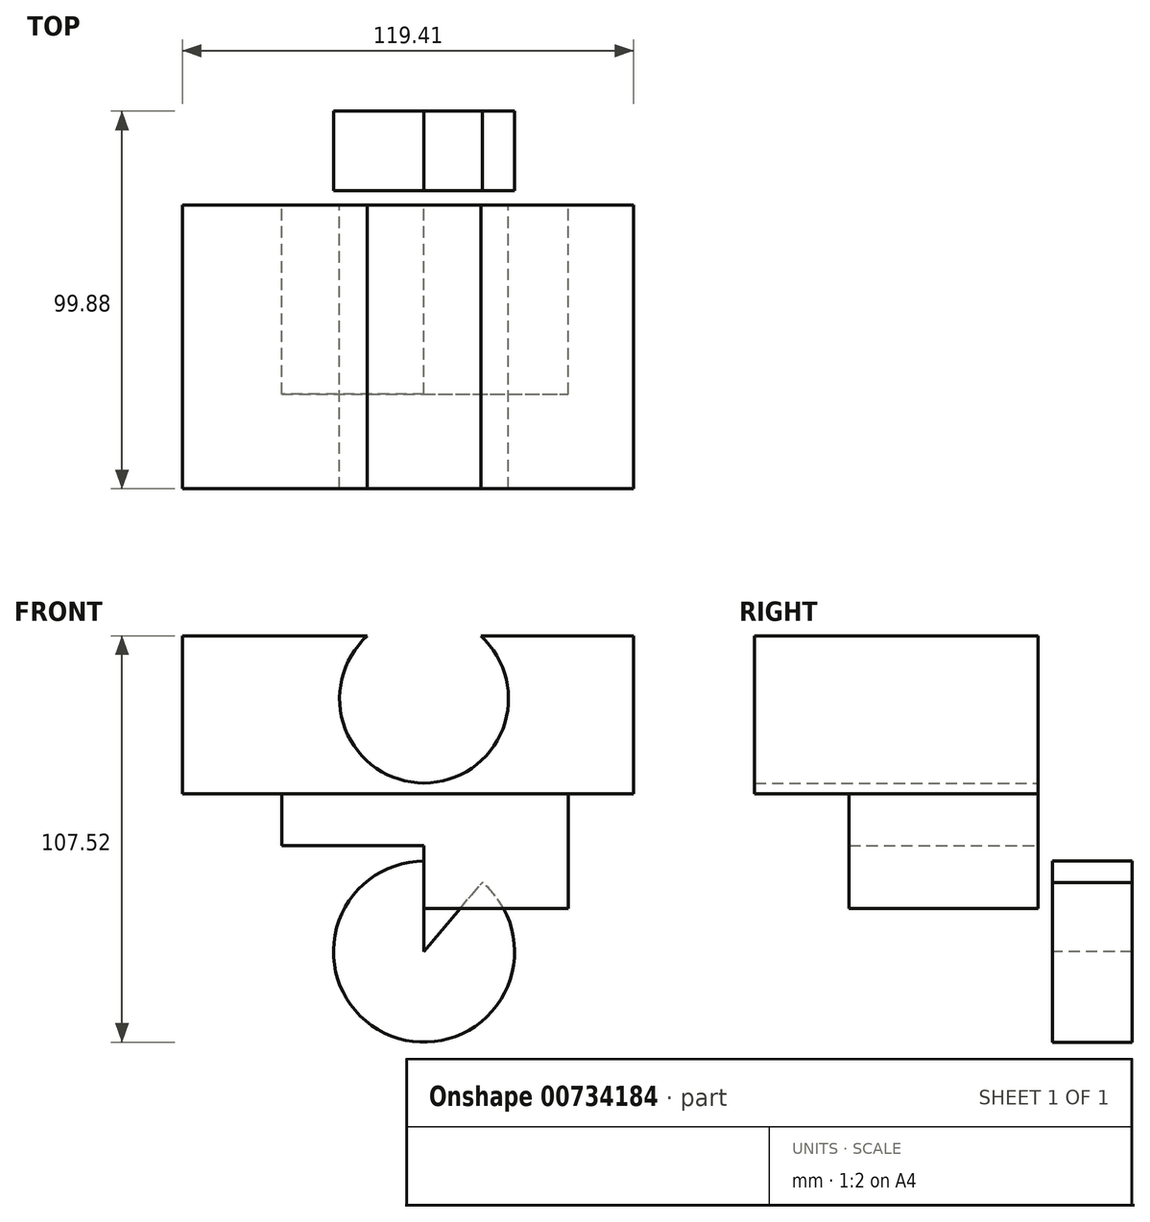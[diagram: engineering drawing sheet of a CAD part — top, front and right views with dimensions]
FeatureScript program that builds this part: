
annotation { "Feature Type Name" : "Feature", "Feature Type Description" : "" }
export const myFeature = defineFeature(function(context is Context, id is Id, definition is map)
    precondition{}
    {
        {
            var Q0;
            Q0=qCreatedBy(makeId("Front.planeOp"),FACE);
            var sketch = newSketch(context, id + "F0", { "sketchPlane" : qUnion([Q0])});
            skLineSegment(sketch, "E0", {"start": v(0, 0) * mm, "end": v(55.5, 0) * mm});
            skLineSegment(sketch, "E1", {"start": v(55.5, 0) * mm, "end": v(55.5, 41.73) * mm});
            skLineSegment(sketch, "E2", {"start": v(55.5, 41.73) * mm, "end": v(-63.9, 41.73) * mm});
            skLineSegment(sketch, "E3", {"start": v(-63.9, 41.73) * mm, "end": v(-63.9, 0) * mm});
            skLineSegment(sketch, "E4", {"start": v(-63.9, 0) * mm, "end": v(0, 0) * mm});
            skSolve(sketch);
        }
        {
            var Q0;
            Q0=qCreatedBy(makeId("Front.planeOp"),FACE);
            var sketch = newSketch(context, id + "F1", { "sketchPlane" : qUnion([Q0])});
            skLineSegment(sketch, "E5.bottom", {"start": v(0, 0) * mm, "end": v(38.22, 0) * mm});
            skLineSegment(sketch, "E5.top", {"start": v(0, -30.35) * mm, "end": v(38.22, -30.35) * mm});
            skLineSegment(sketch, "E5.left", {"start": v(0, 0) * mm, "end": v(0, -30.35) * mm});
            skLineSegment(sketch, "E5.right", {"start": v(38.22, 0) * mm, "end": v(38.22, -30.35) * mm});
            skLineSegment(sketch, "E6.bottom", {"start": v(0, 0) * mm, "end": v(-37.67, 0) * mm});
            skLineSegment(sketch, "E6.top", {"start": v(0, -13.8) * mm, "end": v(-37.67, -13.8) * mm});
            skLineSegment(sketch, "E6.left", {"start": v(0, 0) * mm, "end": v(0, -13.8) * mm});
            skLineSegment(sketch, "E6.right", {"start": v(-37.67, 0) * mm, "end": v(-37.67, -13.8) * mm});
            skSolve(sketch);
        }
        {
            var Q0;
            Q0=makeQuery(id+"F0.imprint","IMPRINT",FACE,{"disambiguationData":[TD([[makeQuery(id+"F0.imprint","IMPRINT",EDGE,{"derivedFrom":sQuery(id+"F0.wireOp",EDGE,"E0")}),1.0]])]});
            var Q1;
            Q1=makeQuery(id+"F1.imprint","IMPRINT",FACE,{"disambiguationData":[TD([[makeQuery(id+"F1.imprint","IMPRINT",EDGE,{"derivedFrom":sQuery(id+"F1.wireOp",EDGE,"E6.bottom")}),1.0]])]});
            var Q2;
            Q2=makeQuery(id+"F1.imprint","IMPRINT",FACE,{"disambiguationData":[TD([[makeQuery(id+"F1.imprint","IMPRINT",EDGE,{"derivedFrom":sQuery(id+"F1.wireOp",EDGE,"E5.bottom")}),-1.0]])]});
            extrude(context, id + "F2", {"entities" : qUnion([Q0, Q1, Q2]), "depth" : 25 * mm, "offsetDistance" : 25 * mm});
        }
        {
            var Q0;
            Q0=makeQuery(id+"F2.opExtrude","CAP_FACE",FACE,{"disambiguationData":[OSD([sQuery(id+"F0.wireOp",EDGE,"E0"),sQuery(id+"F0.wireOp",EDGE,"E1"),sQuery(id+"F0.wireOp",EDGE,"E2"),sQuery(id+"F0.wireOp",EDGE,"E3"),sQuery(id+"F0.wireOp",EDGE,"E4")])],"isStart":false});
            extrude(context, id + "F3", {"entities" : qUnion([Q0]), "operationType" : NewBodyOperationType.ADD, "depth" : 25 * mm, "offsetDistance" : 25 * mm});
        }
        {
            var Q0;
            Q0=makeQuery(id+"F2.opExtrude","CAP_FACE",FACE,{"disambiguationData":[OSD([sQuery(id+"F0.wireOp",EDGE,"E0"),sQuery(id+"F0.wireOp",EDGE,"E1"),sQuery(id+"F0.wireOp",EDGE,"E2"),sQuery(id+"F0.wireOp",EDGE,"E3"),sQuery(id+"F0.wireOp",EDGE,"E4")])],"isStart":true});
            extrude(context, id + "F4", {"entities" : qUnion([Q0]), "operationType" : NewBodyOperationType.ADD, "depth" : 25 * mm, "offsetDistance" : 25 * mm});
        }
        {
            var Q0;
            Q0=makeQuery(id+"F4.opExtrude","CAP_FACE",FACE,{"disambiguationData":[OSD([sQuery(id+"F0.wireOp",EDGE,"E0"),sQuery(id+"F0.wireOp",EDGE,"E1"),sQuery(id+"F0.wireOp",EDGE,"E2"),sQuery(id+"F0.wireOp",EDGE,"E3"),sQuery(id+"F0.wireOp",EDGE,"E4")])],"isStart":false});
            var sketch = newSketch(context, id + "F5", { "sketchPlane" : qUnion([Q0])});
            skCircle(sketch, "E7", {"center": v(0, 25.16) * mm, "radius": 22.36 * mm});
            skSolve(sketch);
        }
        {
            var Q0;
            {var subQ0=sQuery(id+"F5.wireOp",EDGE,"E7");var subQ1=makeQuery(id+"F4.opExtrude","CAP_EDGE",EDGE,{"disambiguationData":[OSD([sQuery(id+"F0.wireOp",EDGE,"E2")])],"isStart":false});var subQ2=makeQuery(id+"F5.imprint","INTERSECT",VERTEX,{"disambiguationData":[OD(0.0)],"derivedFrom":[subQ1,subQ0]});Q0=makeQuery(id+"F5.imprint","IMPRINT",FACE,{"disambiguationData":[TD([[makeQuery(id+"F5.imprint","IMPRINT",EDGE,{"disambiguationData":[TD([[subQ2,1.0]])],"derivedFrom":subQ0}),1.0]])]});}
            var Q1;
            {var subQ0=sQuery(id+"F5.wireOp",EDGE,"E7");var subQ1=makeQuery(id+"F4.opExtrude","CAP_EDGE",EDGE,{"disambiguationData":[OSD([sQuery(id+"F0.wireOp",EDGE,"E2")])],"isStart":false});var subQ2=makeQuery(id+"F5.imprint","INTERSECT",VERTEX,{"disambiguationData":[OD(0.0)],"derivedFrom":[subQ1,subQ0]});Q1=makeQuery(id+"F5.imprint","IMPRINT",FACE,{"disambiguationData":[TD([[makeQuery(id+"F5.imprint","IMPRINT",EDGE,{"disambiguationData":[TD([[subQ2,-1.0]])],"derivedFrom":subQ0}),1.0]])]});}
            var Q2;
            Q2=sQuery(id+"F5.wireOp",EDGE,"E7");
            extrude(context, id + "F6", {"entities" : qUnion([Q0, Q1]), "operationType" : NewBodyOperationType.REMOVE, "surfaceEntities" : qUnion([Q2]), "oppositeDirection" : true, "depth" : 300 * mm, "offsetDistance" : 25 * mm});
        }
        {
            var Q0;
            Q0=qCreatedBy(makeId("Right.planeOp"),FACE);
            var sketch = newSketch(context, id + "F7", { "sketchPlane" : qUnion([Q0])});
            skLineSegment(sketch, "E8.bottom", {"start": v(49.88, -41.84) * mm, "end": v(28.88, -41.84) * mm});
            skLineSegment(sketch, "E8.top", {"start": v(49.88, -17.88) * mm, "end": v(28.88, -17.88) * mm});
            skLineSegment(sketch, "E8.left", {"start": v(49.88, -41.84) * mm, "end": v(49.88, -17.88) * mm});
            skLineSegment(sketch, "E8.right", {"start": v(28.88, -41.84) * mm, "end": v(28.88, -17.88) * mm});
            skSolve(sketch);
        }
        {
            var Q0;
            Q0=makeQuery(id+"F7.imprint","IMPRINT",FACE,{"disambiguationData":[TD([[makeQuery(id+"F7.imprint","IMPRINT",EDGE,{"derivedFrom":sQuery(id+"F7.wireOp",EDGE,"E8.bottom")}),-1.0]])]});
            var Q1;
            Q1=sQuery(id+"F7.wireOp",EDGE,"E8.bottom");
            revolve(context, id + "F8", {"surfaceOperationType" : NewSurfaceOperationType.NEW, "entities" : qUnion([Q0]), "axis" : qUnion([Q1]), "revolveType" : RevolveType.ONE_DIRECTION, "angle" : 320 * degree});
        }
    });
